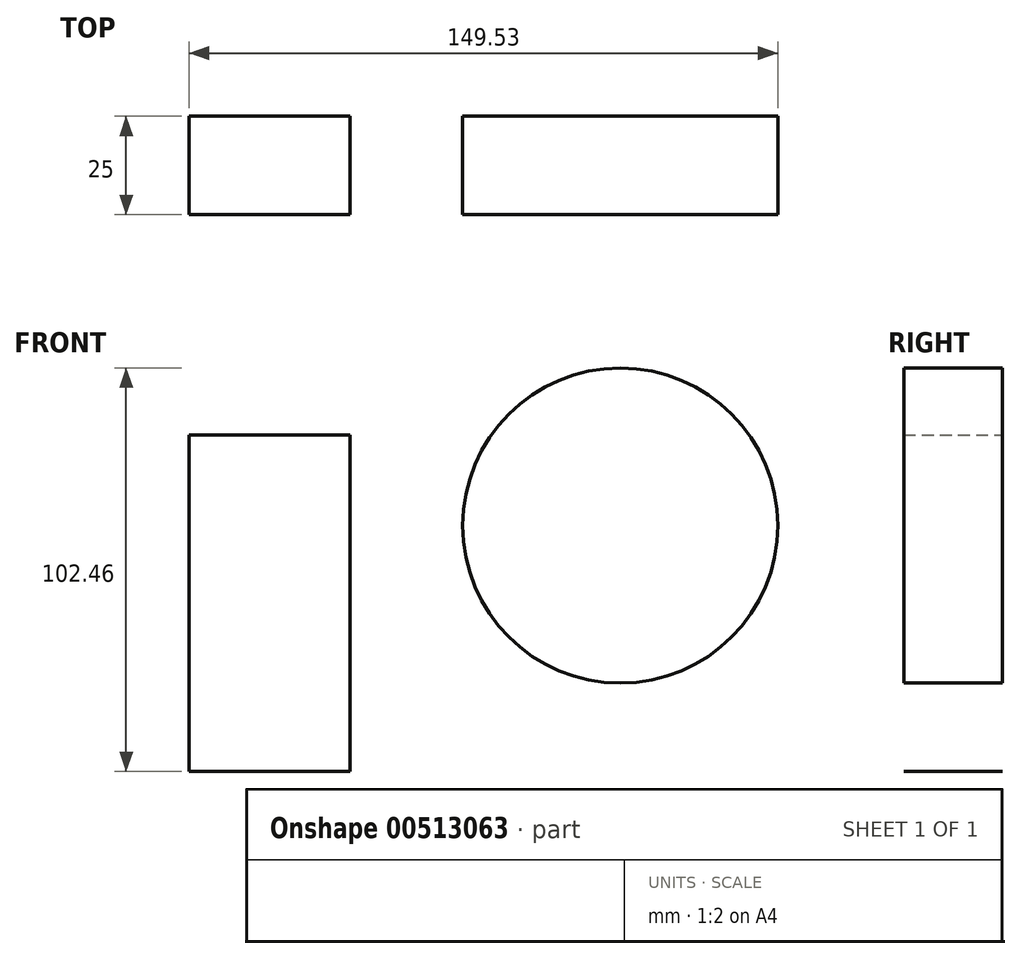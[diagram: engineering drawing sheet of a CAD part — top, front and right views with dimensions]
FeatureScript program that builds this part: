
annotation { "Feature Type Name" : "Feature", "Feature Type Description" : "" }
export const myFeature = defineFeature(function(context is Context, id is Id, definition is map)
    precondition{}
    {
        {
            var Q0;
            Q0=qCreatedBy(makeId("Front.planeOp"),FACE);
            var sketch = newSketch(context, id + "F0", { "sketchPlane" : qUnion([Q0])});
            skLineSegment(sketch, "E0.bottom", {"start": v(-169.2, 45.8) * mm, "end": v(-128.4, 45.8) * mm});
            skLineSegment(sketch, "E0.top", {"start": v(-169.2, -39.62) * mm, "end": v(-128.4, -39.62) * mm});
            skLineSegment(sketch, "E0.left", {"start": v(-169.2, 45.8) * mm, "end": v(-169.2, -39.62) * mm});
            skLineSegment(sketch, "E0.right", {"start": v(-128.4, 45.8) * mm, "end": v(-128.4, -39.62) * mm});
            skCircle(sketch, "E1", {"center": v(-59.7, 22.82) * mm, "radius": 40.03 * mm});
            skSolve(sketch);
        }
        {
            var Q0;
            Q0=makeQuery(id+"F0.imprint","IMPRINT",FACE,{"disambiguationData":[TD([[makeQuery(id+"F0.imprint","IMPRINT",EDGE,{"derivedFrom":sQuery(id+"F0.wireOp",EDGE,"E0.bottom")}),-1.0]])]});
            var Q1;
            Q1=makeQuery(id+"F0.imprint","IMPRINT",FACE,{"disambiguationData":[TD([[makeQuery(id+"F0.imprint","IMPRINT",EDGE,{"derivedFrom":sQuery(id+"F0.wireOp",EDGE,"E1")}),1.0]])]});
            extrude(context, id + "F1", {"entities" : qUnion([Q0, Q1]), "depth" : 25 * mm});
        }
    });
